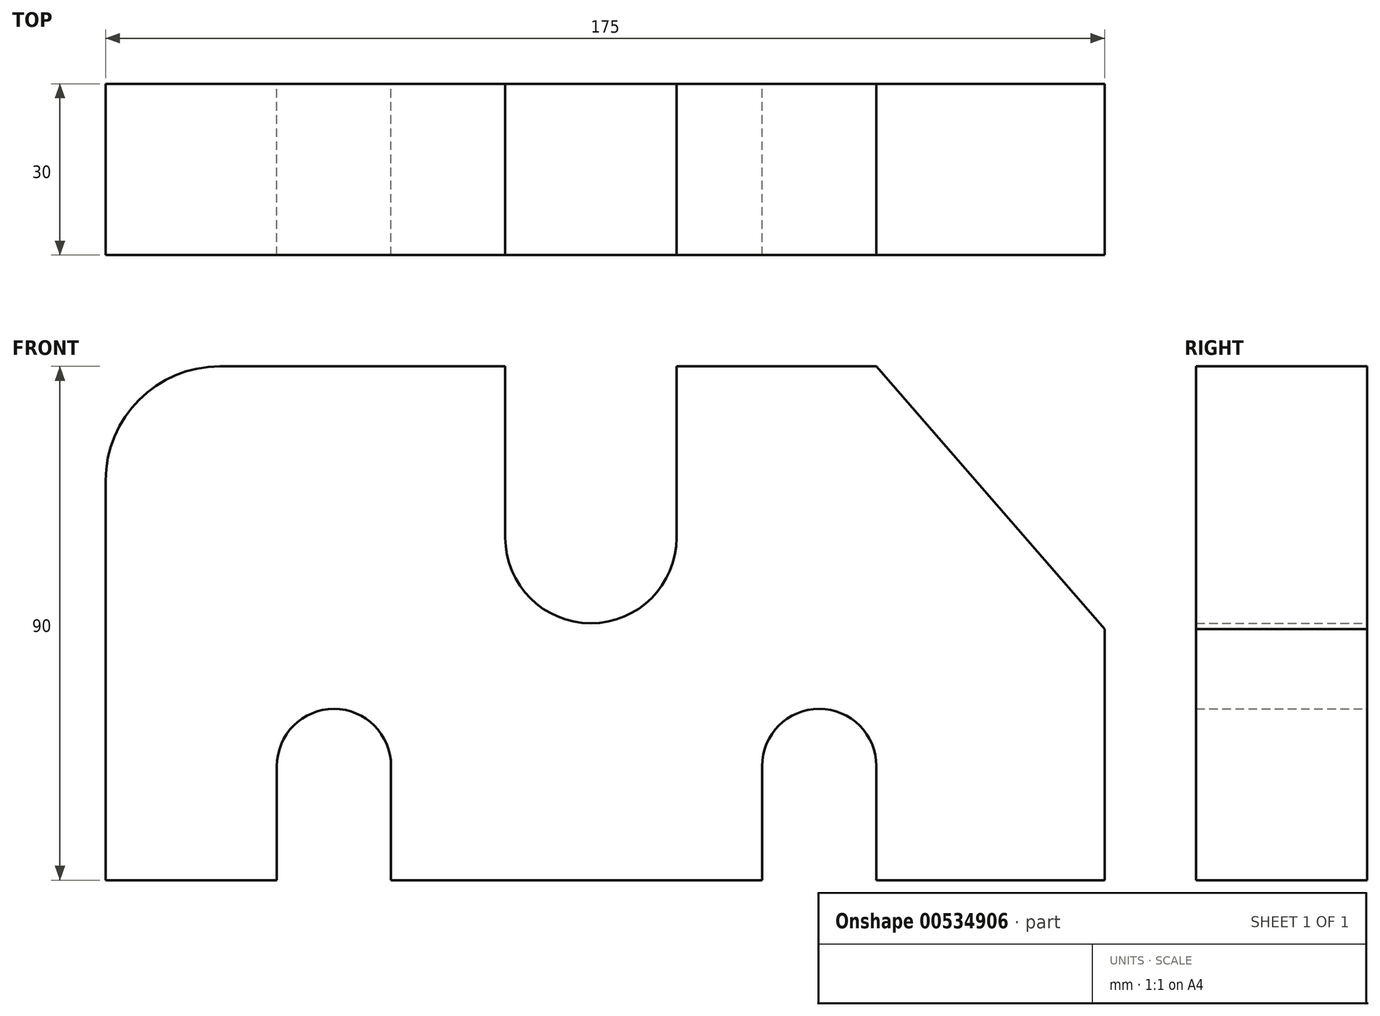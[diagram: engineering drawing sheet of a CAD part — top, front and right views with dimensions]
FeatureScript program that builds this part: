
annotation { "Feature Type Name" : "Feature", "Feature Type Description" : "" }
export const myFeature = defineFeature(function(context is Context, id is Id, definition is map)
    precondition{}
    {
        {
            var Q0;
            Q0=qCreatedBy(makeId("Front.planeOp"),FACE);
            var sketch = newSketch(context, id + "F0", { "sketchPlane" : qUnion([Q0])});
            skLineSegment(sketch, "E0", {"start": v(0, 0) * mm, "end": v(0, 70) * mm});
            skLineSegment(sketch, "E1", {"start": v(20, 90) * mm, "end": v(70, 90) * mm});
            skLineSegment(sketch, "E2", {"start": v(70, 90) * mm, "end": v(70, 60) * mm});
            skArc(sketch, "E3", {"start": v(70, 60) * mm, "mid": v(85, 45) * mm, "end": v(100, 60) * mm});
            skLineSegment(sketch, "E4", {"start": v(100, 60) * mm, "end": v(100, 90) * mm});
            skLineSegment(sketch, "E5", {"start": v(100, 90) * mm, "end": v(135, 90) * mm});
            skLineSegment(sketch, "E6", {"start": v(135, 90) * mm, "end": v(175, 44) * mm});
            skLineSegment(sketch, "E7", {"start": v(175, 44) * mm, "end": v(175, 0) * mm});
            skLineSegment(sketch, "E8", {"start": v(175, 0) * mm, "end": v(135, 0) * mm});
            skLineSegment(sketch, "E9", {"start": v(135, 0) * mm, "end": v(135, 20) * mm});
            skArc(sketch, "E10", {"start": v(135, 20) * mm, "mid": v(125, 30) * mm, "end": v(115, 20) * mm});
            skLineSegment(sketch, "E11", {"start": v(115, 20) * mm, "end": v(115, 0) * mm});
            skLineSegment(sketch, "E12", {"start": v(115, 0) * mm, "end": v(50, 0) * mm});
            skLineSegment(sketch, "E13", {"start": v(50, 0) * mm, "end": v(50, 20) * mm});
            skArc(sketch, "E14", {"start": v(50, 20) * mm, "mid": v(40, 30) * mm, "end": v(30, 20) * mm});
            skLineSegment(sketch, "E15", {"start": v(30, 20) * mm, "end": v(30, 0) * mm});
            skLineSegment(sketch, "E16", {"start": v(30, 0) * mm, "end": v(0, 0) * mm});
            skPoint(sketch, "E17.visualSharp", {"position": v(0, 90) * mm});
            skArc(sketch, "E17.filletArc", {"start": v(20, 90) * mm, "mid": v(5.86, 84.14) * mm, "end": v(0, 70) * mm});
            skSolve(sketch);
        }
        {
            var Q0;
            Q0 = qSketchRegion(id + "F0", true);
            extrude(context, id + "F1", {"entities" : qUnion([Q0]), "depth" : 30 * mm, "offsetDistance" : 25 * mm});
        }
    });
